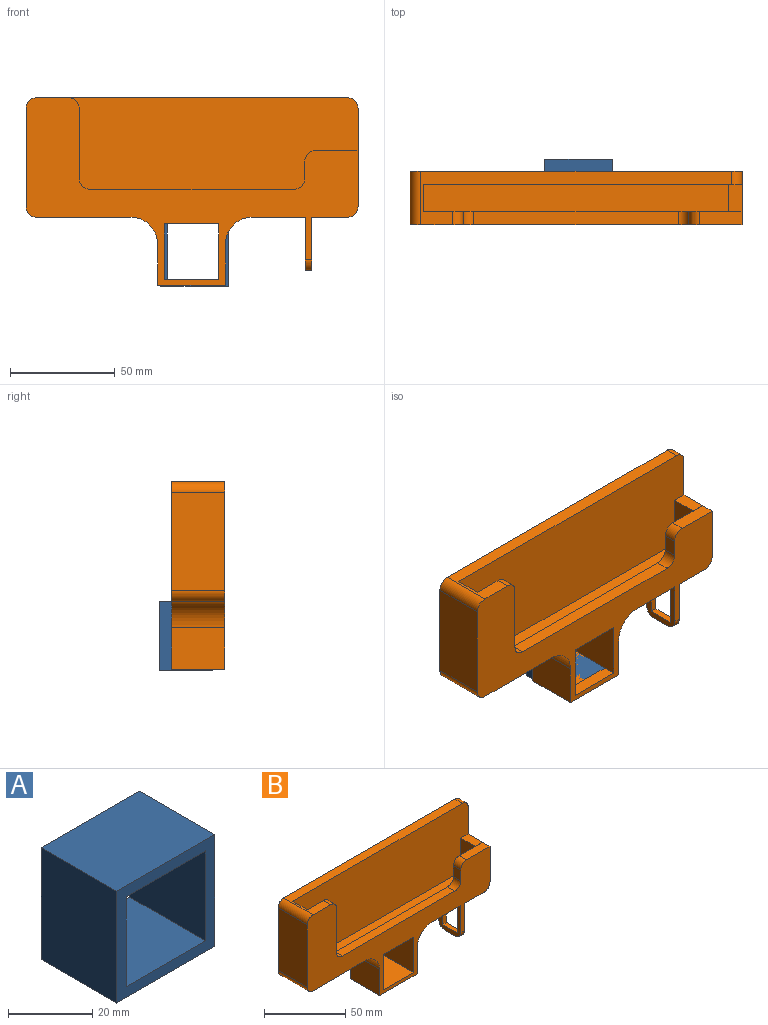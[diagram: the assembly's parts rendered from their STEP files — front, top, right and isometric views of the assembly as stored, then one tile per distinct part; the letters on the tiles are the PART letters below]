
ASSEMBLY  parts=2 mates=1
PART A: 10 faces, bbox 33x25.4x32.5 mm
  f0: plane 26.67x25.4mm, normal (0,0,1), area 677.4mm2, adj f1,f7,f8,f9
  f1: plane 26.16x25.4mm, normal (1,0,0), area 664.5mm2, adj f0,f2,f8,f9
  f2: plane 26.67x25.4mm, normal (0,0,-1), area 677.4mm2, adj f1,f7,f8,f9
  f3: plane 32.51x25.4mm, normal (-1,0,0), area 825.8mm2, adj f4,f6,f8,f9
  f4: plane 33.02x25.4mm, normal (0,0,-1), area 838.7mm2, adj f3,f5,f8,f9
  f5: plane 32.51x25.4mm, normal (1,0,0), area 825.8mm2, adj f4,f6,f8,f9
  f6: plane 33.02x25.4mm, normal (0,0,1), area 838.7mm2, adj f3,f5,f8,f9
  f7: plane 26.16x25.4mm, normal (-1,0,0), area 664.5mm2, adj f0,f2,f8,f9
  f8: plane 33.02x32.51mm, normal (0,-1,0), area 375.8mm2, adj f0,f1,f2,f3,f4,f5,f6,f7
  f9: plane 33.02x32.51mm, normal (0,1,0), area 375.8mm2, adj f0,f1,f2,f3,f4,f5,f6,f7
PART B: 47 faces, bbox 158.8x25.4x89.7 mm
  f0: plane 158.75x89.66mm, normal (0,1,0), area 9478.9mm2, adj f2,f4,f5,f6,f7,f17,f18,f19
  f1: plane 158.75x89.66mm, normal (0,-1,0), area 4185.1mm2, adj f2,f4,f5,f6,f7,f12,f13,f14
  f2: plane 45.57x25.4mm, normal (0,0,-1), area 1147.4mm2, adj f0,f1,f24,f29,f33,f34,f46
  f3: plane 152.4x50.8mm, normal (0,-1,0), area 7575.1mm2, adj f6,f7,f8,f9,f10,f11,f43
  f4: plane 46.99x25.4mm, normal (-1,0,0), area 1193.5mm2, adj f0,f1,f44,f45
  f5: plane 45.11x25.4mm, normal (0,0,-1), area 1145.7mm2, adj f0,f1,f25,f45
  f6: plane 46.99x25.4mm, normal (1,0,0), area 806.5mm2, adj f0,f1,f3,f9,f12,f43,f46
  f7: plane 148.59x25.4mm, normal (0,0,1), area 1056.4mm2, adj f0,f1,f3,f8,f16,f39,f43,f44
  f8: plane 50.8x12.7mm, normal (1,0,0), area 645.2mm2, adj f3,f7,f11,f16
  f9: plane 12.7x6.35mm, normal (0,0,1), area 80.6mm2, adj f3,f6,f10,f16
  f10: plane 25.4x12.7mm, normal (-1,0,0), area 322.6mm2, adj f3,f9,f11,f16
  f11: plane 146.05x12.7mm, normal (0,0,1), area 1854.8mm2, adj f3,f8,f10,f16
  f12: plane 20.3x6.35mm, normal (0,0,1), area 128.9mm2, adj f1,f6,f16,f40
  f13: plane 8.25x6.35mm, normal (-1,0,0), area 52.4mm2, adj f1,f16,f40,f41
  f14: plane 97.79x6.35mm, normal (0,0,1), area 621mm2, adj f1,f16,f41,f42
  f15: plane 33.57x6.35mm, normal (1,0,0), area 213.1mm2, adj f1,f16,f39,f42
  f16: plane 152.4x50.8mm, normal (0,1,0), area 2216.7mm2, adj f7,f8,f9,f10,f11,f12,f13,f14
  f17: plane 25.4x19.81mm, normal (-1,0,0), area 503.2mm2, adj f0,f1,f19,f25
  f18: plane 25.4x19.81mm, normal (1,0,0), area 503.2mm2, adj f0,f1,f19,f24
  f19: plane 32.51x25.4mm, normal (0,0,-1), area 825.8mm2, adj f0,f1,f17,f18
  f20: plane 26.67x25.4mm, normal (1,0,0), area 677.4mm2, adj f0,f1,f21,f23
  f21: plane 26.16x25.4mm, normal (0,0,1), area 664.5mm2, adj f0,f1,f20,f22
  f22: plane 26.67x25.4mm, normal (-1,0,0), area 677.4mm2, adj f0,f1,f21,f23
  f23: plane 26.16x25.4mm, normal (0,0,-1), area 664.5mm2, adj f0,f1,f20,f22
  f24: cylinder r=12.7mm len=25.4mm, axis (0,1,0), area 506.7mm2, adj f0,f1,f2,f18
  f25: cylinder r=12.7mm len=25.4mm, axis (0,-1,0), area 506.7mm2, adj f0,f1,f5,f17
  f26: plane 3.18x1.64mm, normal (0,0,-1), area 5.2mm2, adj f27,f33,f34,f36
  f27: plane 12.7x3.18mm, normal (0,-1,0), area 40.3mm2, adj f26,f28,f33,f34
  f28: plane 12.7x3.18mm, normal (0,0,1), area 40.3mm2, adj f27,f29,f33,f34
  f29: plane 22.23x3.18mm, normal (0,1,0), area 70.6mm2, adj f2,f28,f33,f34
  f30: plane 8.89x3.18mm, normal (0,0,-1), area 28.2mm2, adj f33,f34,f35,f37
  f31: plane 8.89x3.18mm, normal (0,1,0), area 28.2mm2, adj f33,f34,f37,f38
  f32: plane 4.45x3.18mm, normal (0,0,1), area 14.1mm2, adj f33,f34,f36,f38
  f33: plane 25.4x19.05mm, normal (1,0,0), area 180.9mm2, adj f1,f2,f26,f27,f28,f29,f30,f31
  f34: plane 25.4x19.05mm, normal (-1,0,0), area 180.9mm2, adj f1,f2,f26,f27,f28,f29,f30,f31
  f35: cylinder r=5.08mm len=5.08mm, axis (1,0,0), area 25.3mm2, adj f1,f30,f33,f34
  f36: cylinder r=5.08mm len=4.71mm, axis (1,0,0), area 19.1mm2, adj f26,f32,f33,f34
  f37: cylinder r=5.08mm len=5.08mm, axis (1,0,0), area 25.3mm2, adj f30,f31,f33,f34
  f38: cylinder r=5.08mm len=5.08mm, axis (-1,0,0), area 25.3mm2, adj f31,f32,f33,f34
  f39: cylinder r=5.08mm len=6.35mm, axis (0,1,0), area 50.7mm2, adj f1,f7,f15,f16
  f40: cylinder r=5.08mm len=6.35mm, axis (0,1,0), area 50.8mm2, adj f1,f12,f13,f16
  f41: cylinder r=5.08mm len=6.35mm, axis (0,-1,0), area 50.7mm2, adj f1,f13,f14,f16
  f42: cylinder r=5.08mm len=6.35mm, axis (0,-1,0), area 50.7mm2, adj f1,f14,f15,f16
  f43: cylinder r=5.08mm len=6.35mm, axis (0,-1,0), area 50.7mm2, adj f0,f3,f6,f7
  f44: cylinder r=5.08mm len=25.4mm, axis (0,1,0), area 202.7mm2, adj f0,f1,f4,f7
  f45: cylinder r=5.08mm len=25.4mm, axis (0,-1,0), area 202.7mm2, adj f0,f1,f4,f5
  f46: cylinder r=5.08mm len=25.4mm, axis (0,1,0), area 202.7mm2, adj f0,f1,f2,f6
PLACE A rot(axis=(0,-1,0),90deg) t=(35.72,39.11,-52.32)mm
PLACE B t=(-58,33.11,-22.48)mm
MATE planar A.f5 <-> B.f5  axis (0,0,1) through (22.64,26.41,-22.48)mm
